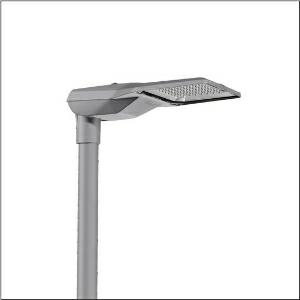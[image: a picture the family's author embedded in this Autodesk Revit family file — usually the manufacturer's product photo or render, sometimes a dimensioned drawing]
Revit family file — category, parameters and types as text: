
# Revit family: streetlight_sl_21_midi___p0_8a_5xe3u33s08nb_1026
name_source: partatom
category: Lighting Fixtures
units: mm (PartAtom-declared; Revit-internal decimal feet)

## family parameters
Cut with Voids When Loaded = No
Host = Face
Light Source = No
Part Type = Normal
Room Calculation Point = No
Round Connector Dimension = Use Diameter
Shared = No

## types (1)
- --- (1 x LED, 22900 lm, 151.2 W, 3000K)
    Apparent Load = 151 VA
    CIE Flux Codes = 36 69 97 100 100
    Color Rendering = 70
    Color Temperature = 3000K
    Default Elevation = 1800 mm
    Description = Streetlight SL 21 midi, mast luminaire, primary light control with lens, of PMMA, primary optical cover: cover, of toughened safety glass, transparent, light distribution: P0.8a, light emission: direct distribution, primary light characteristic: asymmetric, installation type: post-top, side-entry, LED, High Power LED, rated luminous flux: 22.900lm, luminous efficacy: 152lm/W, light colour: 730, colour temperature: 3000K, control gear: D4i, control: pre-setting: logarithmic dimming characteristic, flexible luminous flux parameterisation, time-dependent luminous flux control, constant luminous flux control, overheat protection, mains connection: 230..240V, AC, 50/60Hz, start of lifetime: 151W, end of service life: 157W, reduction: 70W, luminaire housing, of diecast aluminium, powder-coated, Siteco® metallic grey (DB 702S), corrosivity category C5 mid according to DIN EN ISO 12944, multi-level sealing system, sealing non-destructively replaceable, inclination adjustable: 0°, 5°, 10°, 15°, please order mast flange separately, length: 644mm, width: 335mm, height: 110mm, mast flange for spigot size: 42mm (side-entry): 5XC10008XM4, 60/48mm (side-entry/post-top): 5XC10108XM2, 76/60mm (side-entry/post-top): 5XC10108XM1, mounting height: 4..8m, Smart Interface above, protection rating (complete): IP66, insulation class (complete): insulation class II (safety insulation), certification: CE, ENEC, ENEC+, VDE, impact resistance: IK10, permissible operating ambient temperature for outdoor applications: -40..+50°C, standard-compliant lighting for roads and squares, packaging unit: 1 piece

Light Distribution: P0.8a
    Height = 111 mm
    Lamp = 1 x LED
    Lamp Light Flux = 22900 lm
    Lamp Power = 151.2 W
    Lamp count = 1
    Length = 644 mm
    Luminous efficacy = 151 lm/W
    Manufacturer = Siteco
    ModVariant = No
    Model = 5XE3U33S08NB
    Number of Poles = 1
    OnlyDefault = Yes
    Power Factor = 1
    Product Name = Streetlight SL 21 midi | P0.8a
    Product group = mast luminaire | pylon top
    ProductGroupID = 6100
    Protection Class = Protection class II
    Protection Degree = IP 66
    RLX_Detail_Level = 1
    RLX_Emergency_Light_Flux = 0 lm
    RLX_Emergency_Type = 0
    RLX_Emergency_Type_DB = No
    RlxData = <blob elided: 91013 chars, md5=f22d103b>
    Socket = socket
    Standby Power = 0 W
    System Light Flux = 22901 lm
    System Power = 151 W
    Type Comments = factory setting: luminous flux: 100 % | dim-lin: 254 | 802 mA
    Type Image = l_1004302.jpg
    URL = http://relux.com
    VarID = @adj_092963
    Voltage = 0 V
    Weight = 0.00 kg
    Width = 336 mm

## geometry (parser evidence)
native form markers: Blend x4, Sweep x12
no freeform markers — native parametric forms only
